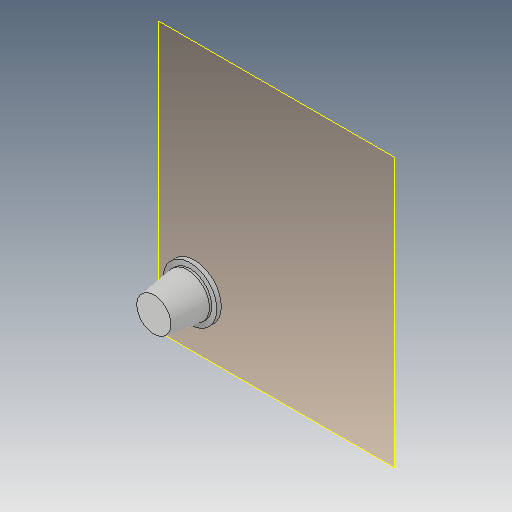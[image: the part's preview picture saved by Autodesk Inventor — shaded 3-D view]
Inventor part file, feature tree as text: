
AUTODESK INVENTOR PART (.ipt)
format: ipt  version: 2017 (Build 210142000, 142)  size: 112,128 bytes
history: native  units: mm
features: other x7, extrude x2, sketch x2, chamfer x1, plane x1, reference x1
ambient origin geometry x8: Origin, YZ Plane, XZ Plane, XY Plane, X Axis, Y Axis, Z Axis, Center Point
bodies: Solid1 (feature_tree)
feature tree (14):
  extrude  "Extrusion1"  Depth=2.0mm
  chamfer  "Chamfer2"  Distance=2.0mm
  plane  "Work Plane1"
  extrude  "Extrusion2"  [1 undecoded]
  sketch  "Sketch1"  dims[d0=18.0mm d1=0.0mm d5=15.0mm d6=2.0mm d7=1.396263mm d8=2.0mm d9=0.0mm]
  reference  "Reference1"
  sketch  "Sketch2"
  parser-record x2  (decoder bookkeeping rows leaked as tree rows — omitted from the tree; the rows remain in map.json)
  other  "LCD Mount Front.iam"
  other  "Smart-ControllerandBracket:1"
  other  "Full Graphic Smart Controller:1"
  other  "LCD-Mount.iam"
  other  "LCD-Front:1"
note: 1 required parameter value undecoded (feature->parameter linkage not recoverable at this tier; creation-order binding heuristic only, values carry confidence <= 0.55)
note: 2 file-system paths scrubbed to <path> (originals preserved in map.json)
